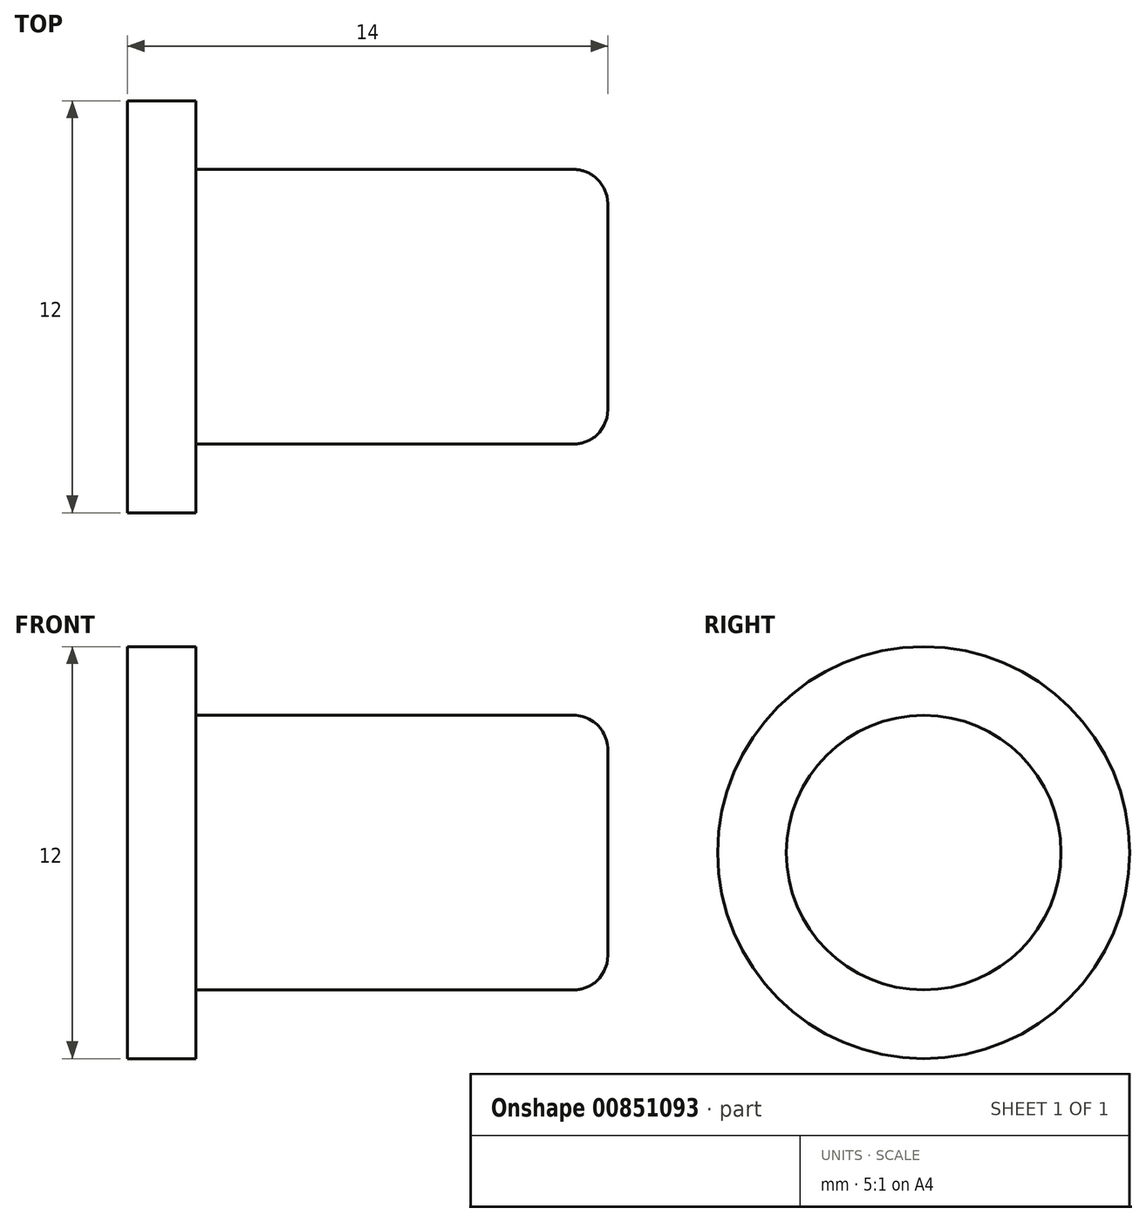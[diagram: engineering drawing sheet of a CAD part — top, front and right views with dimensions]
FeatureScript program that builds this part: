
annotation { "Feature Type Name" : "Feature", "Feature Type Description" : "" }
export const myFeature = defineFeature(function(context is Context, id is Id, definition is map)
    precondition{}
    {
        {
            var Q0;
            Q0=qCreatedBy(makeId("Top.planeOp"),FACE);
            var sketch = newSketch(context, id + "F0", { "sketchPlane" : qUnion([Q0])});
            skLineSegment(sketch, "E0.bottom", {"start": v(0, 0) * mm, "end": v(2, 0) * mm});
            skLineSegment(sketch, "E0.top", {"start": v(0, -6) * mm, "end": v(2, -6) * mm});
            skLineSegment(sketch, "E0.left", {"start": v(0, 0) * mm, "end": v(0, -6) * mm});
            skLineSegment(sketch, "E0.right", {"start": v(2, -4) * mm, "end": v(2, -6) * mm});
            skLineSegment(sketch, "E1.bottom", {"start": v(2, 0) * mm, "end": v(14, 0) * mm});
            skLineSegment(sketch, "E1.top", {"start": v(2, -4) * mm, "end": v(14, -4) * mm});
            skLineSegment(sketch, "E1.right", {"start": v(14, 0) * mm, "end": v(14, -4) * mm});
            skLineSegment(sketch, "E2", {"start": v(-7.8, 0) * mm, "end": v(22.43, 0) * mm, "construction": true});
            skSolve(sketch);
        }
        {
            var Q0;
            Q0=makeQuery(id+"F0.imprint","IMPRINT",FACE,{"disambiguationData":[TD([[makeQuery(id+"F0.imprint","IMPRINT",EDGE,{"derivedFrom":sQuery(id+"F0.wireOp",EDGE,"E0.bottom")}),-1.0]])]});
            var Q1;
            Q1=sQuery(id+"F0.wireOp",EDGE,"E2");
            revolve(context, id + "F1", {"surfaceOperationType" : NewSurfaceOperationType.NEW, "entities" : qUnion([Q0]), "axis" : qUnion([Q1]), "revolveType" : RevolveType.FULL});
        }
        {
            var Q0;
            Q0=makeQuery(id+"F1.opRevolve","SWEPT_EDGE",EDGE,{"disambiguationData":[OSD([sQuery(id+"F0.wireOp",EDGE,"E1.top"),sQuery(id+"F0.wireOp",EDGE,"E1.right")])]});
            fillet(context, id + "F2", {"entities" : qUnion([Q0]), "radius" : 1 * mm, "tangentPropagation" : true, "allowEdgeOverflow" : false});
        }
    });
